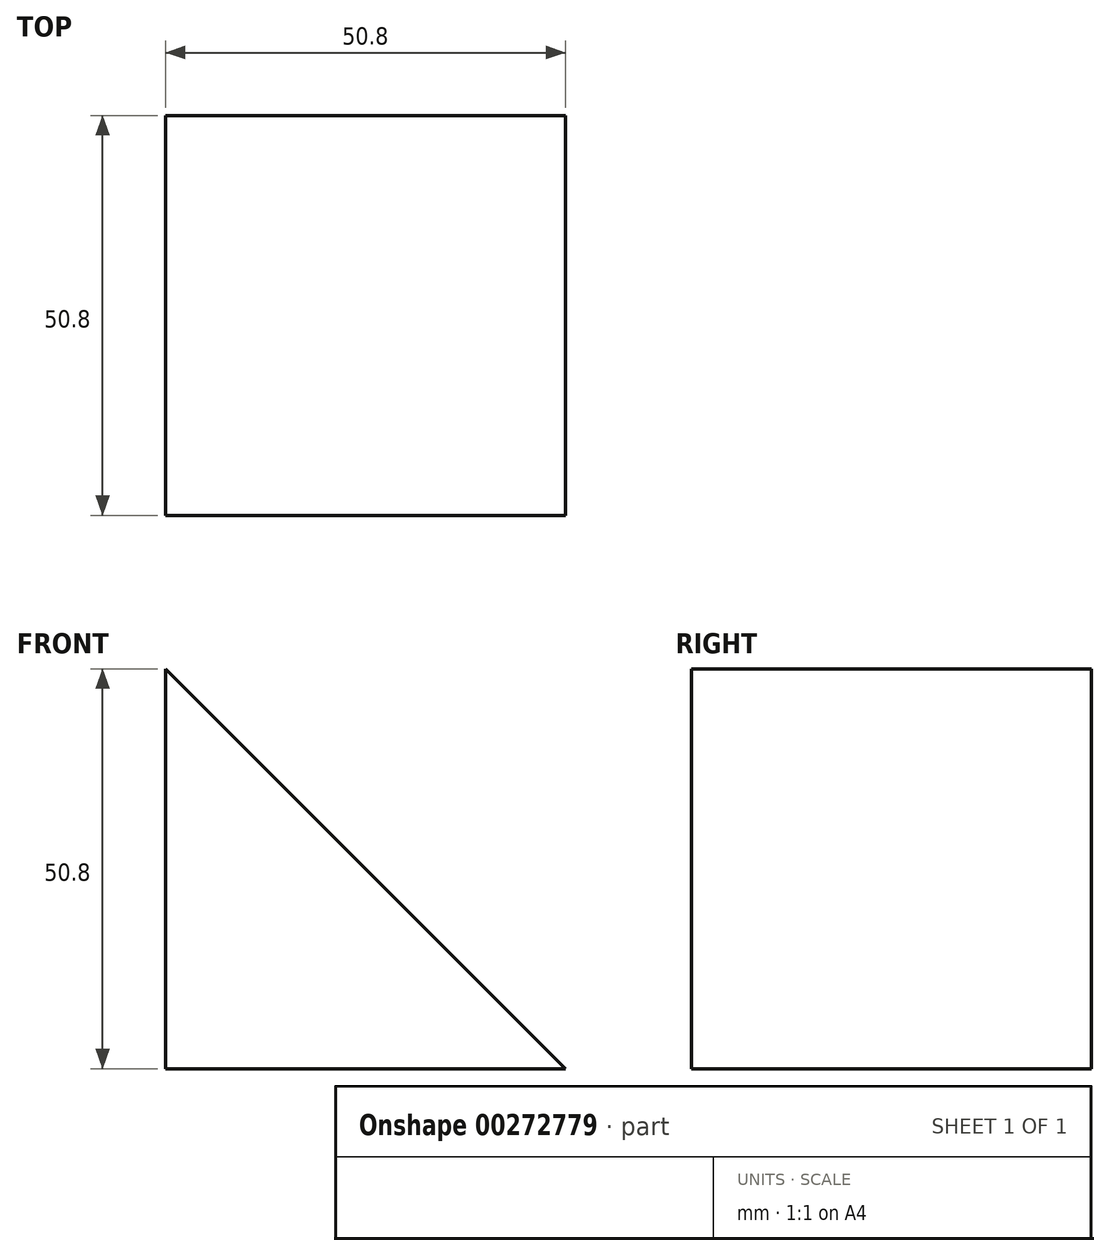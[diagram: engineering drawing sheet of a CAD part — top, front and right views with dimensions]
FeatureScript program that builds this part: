
annotation { "Feature Type Name" : "Feature", "Feature Type Description" : "" }
export const myFeature = defineFeature(function(context is Context, id is Id, definition is map)
    precondition{}
    {
        {
            var Q0;
            Q0=qCreatedBy(makeId("Front.planeOp"),FACE);
            var sketch = newSketch(context, id + "F0", { "sketchPlane" : qUnion([Q0])});
            skLineSegment(sketch, "E0", {"start": v(-59.7, 0) * mm, "end": v(-59.7, 50.8) * mm});
            skLineSegment(sketch, "E1", {"start": v(-59.7, 50.8) * mm, "end": v(-8.9, 0) * mm});
            skLineSegment(sketch, "E2", {"start": v(-59.7, 0) * mm, "end": v(-8.9, 0) * mm});
            skSolve(sketch);
        }
        {
            var Q0;
            Q0 = qSketchRegion(id + "F0", true);
            extrude(context, id + "F1", {"entities" : qUnion([Q0]), "depth" : 50.8 * mm});
        }
    });
